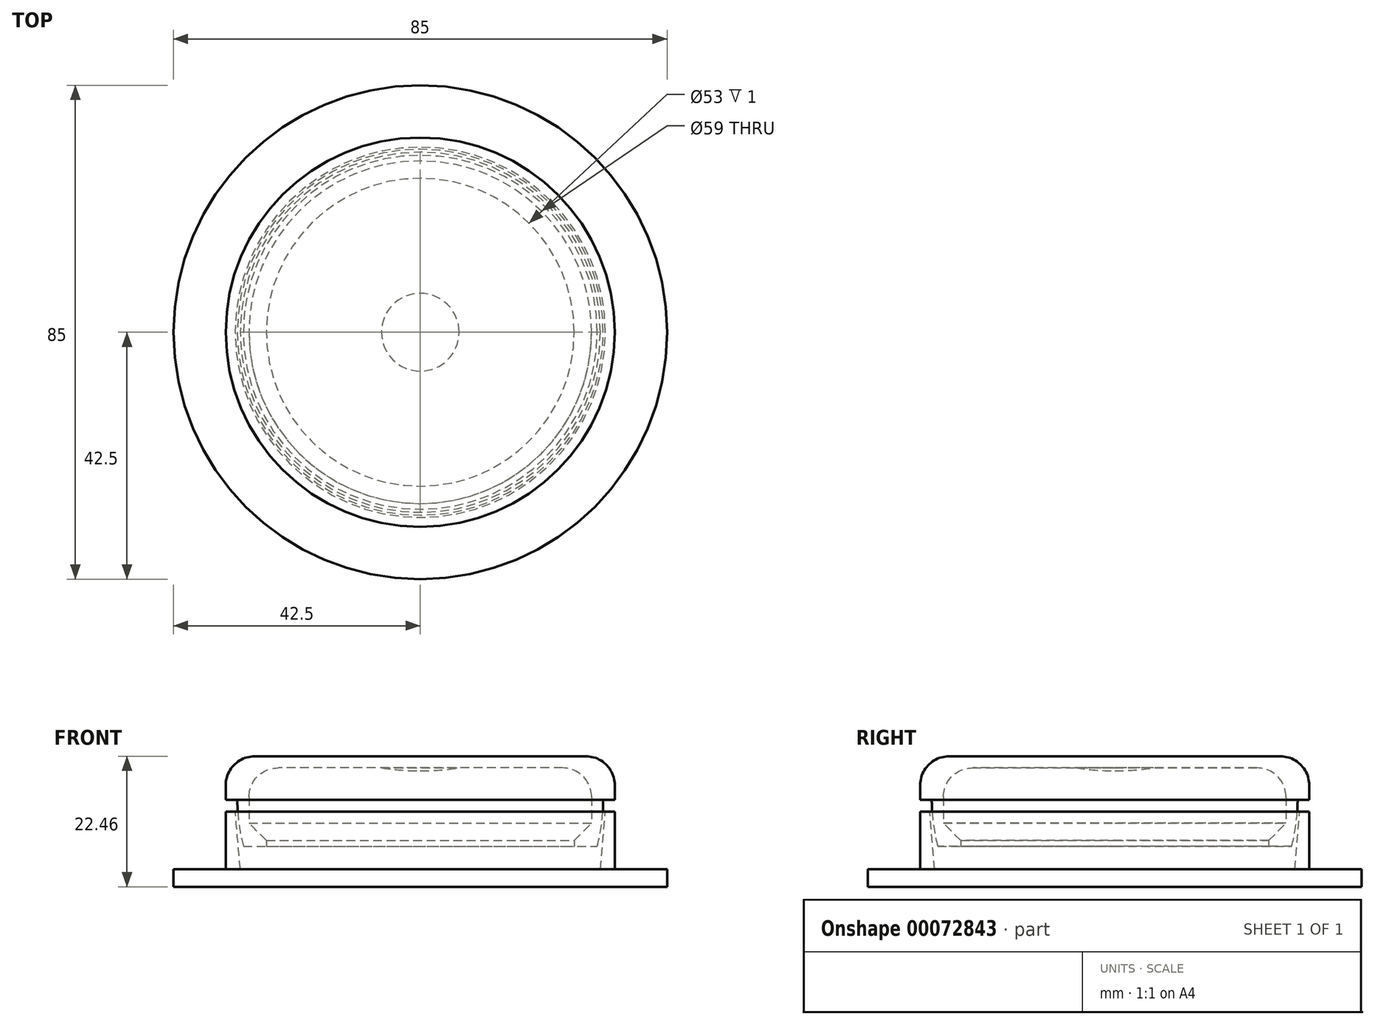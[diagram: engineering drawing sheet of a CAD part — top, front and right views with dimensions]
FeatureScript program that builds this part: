
annotation { "Feature Type Name" : "Feature", "Feature Type Description" : "" }
export const myFeature = defineFeature(function(context is Context, id is Id, definition is map)
    precondition{}
    {
        {
            var Q0;
            Q0=qCreatedBy(makeId("Front.planeOp"),FACE);
            var sketch = newSketch(context, id + "F0", { "sketchPlane" : qUnion([Q0])});
            skLineSegment(sketch, "E0", {"start": v(0, 0) * mm, "end": v(-33.5, 0) * mm});
            skLineSegment(sketch, "E1", {"start": v(-33.5, 0) * mm, "end": v(-33.5, -7.5) * mm});
            skLineSegment(sketch, "E2", {"start": v(-33.5, -7.5) * mm, "end": v(-31.5, -7.5) * mm});
            skArc(sketch, "E3", {"start": v(-31.5, -7.5) * mm, "mid": v(-31.24, -11.53) * mm, "end": v(-30.47, -15.5) * mm});
            skLineSegment(sketch, "E4", {"start": v(-30.47, -15.5) * mm, "end": v(-26.5, -15.5) * mm});
            skLineSegment(sketch, "E5", {"start": v(-26.5, -15.5) * mm, "end": v(-26.5, -14.5) * mm});
            skLineSegment(sketch, "E6", {"start": v(-26.5, -14.5) * mm, "end": v(-29.5, -11.5) * mm});
            skLineSegment(sketch, "E7", {"start": v(-29.5, -11.5) * mm, "end": v(-29.5, -2) * mm});
            skLineSegment(sketch, "E8", {"start": v(-29.5, -2) * mm, "end": v(-6.69, -2) * mm});
            skLineSegment(sketch, "E9", {"start": v(-31.5, -7.5) * mm, "end": v(-31.5, -25.68) * mm, "construction": true});
            skLineSegment(sketch, "E10", {"start": v(-31.5, -7.5) * mm, "end": v(0, -7.5) * mm, "construction": true});
            skArc(sketch, "E11", {"start": v(-6.69, -2) * mm, "mid": v(-3.35, -2.37) * mm, "end": v(0, -2.5) * mm});
            skLineSegment(sketch, "E12", {"start": v(0, -2.5) * mm, "end": v(0, 0) * mm});
            skSolve(sketch);
        }
        {
            var Q0;
            Q0 = qSketchRegion(id + "F0", true);
            var Q1;
            Q1=sQuery(id+"F0.wireOp",EDGE,"E12");
            revolve(context, id + "F1", {"entities" : qUnion([Q0]), "axis" : qUnion([Q1]), "revolveType" : RevolveType.FULL});
        }
        {
            var Q0;
            Q0=makeQuery(id+"F1.opRevolve","SWEPT_EDGE",EDGE,{"disambiguationData":[OSD([sQuery(id+"F0.wireOp",EDGE,"E7"),sQuery(id+"F0.wireOp",EDGE,"E8")])]});
            var Q1;
            Q1=makeQuery(id+"F1.opRevolve","SWEPT_EDGE",EDGE,{"disambiguationData":[OSD([sQuery(id+"F0.wireOp",EDGE,"E0"),sQuery(id+"F0.wireOp",EDGE,"E1")])]});
            fillet(context, id + "F2", {"entities" : qUnion([Q0, Q1]), "radius" : 5 * mm, "tangentPropagation" : true, "allowEdgeOverflow" : false});
        }
        {
            var Q0;
            Q0=qCreatedBy(makeId("Right.planeOp"),FACE);
            var sketch = newSketch(context, id + "F3", { "sketchPlane" : qUnion([Q0])});
            skLineSegment(sketch, "E13", {"start": v(0, -19.46) * mm, "end": v(-31, -19.46) * mm});
            skLineSegment(sketch, "E14", {"start": v(-31, -19.46) * mm, "end": v(-31.87, -9.5) * mm});
            skLineSegment(sketch, "E15", {"start": v(-31.87, -9.5) * mm, "end": v(-33.5, -9.5) * mm});
            skLineSegment(sketch, "E16", {"start": v(-33.5, -9.5) * mm, "end": v(-33.5, -19.46) * mm});
            skLineSegment(sketch, "E17", {"start": v(-33.5, -19.46) * mm, "end": v(-42.5, -19.46) * mm});
            skLineSegment(sketch, "E18", {"start": v(-42.5, -19.46) * mm, "end": v(-42.5, -22.46) * mm});
            skLineSegment(sketch, "E19", {"start": v(-42.5, -22.46) * mm, "end": v(0, -22.46) * mm});
            skLineSegment(sketch, "E20", {"start": v(0, -22.46) * mm, "end": v(0, -19.46) * mm});
            skSolve(sketch);
        }
        {
            var Q0;
            Q0 = qSketchRegion(id + "F3", true);
            var Q1;
            Q1=sQuery(id+"F3.wireOp",EDGE,"E20");
            revolve(context, id + "F4", {"entities" : qUnion([Q0]), "axis" : qUnion([Q1]), "revolveType" : RevolveType.FULL});
        }
    });
